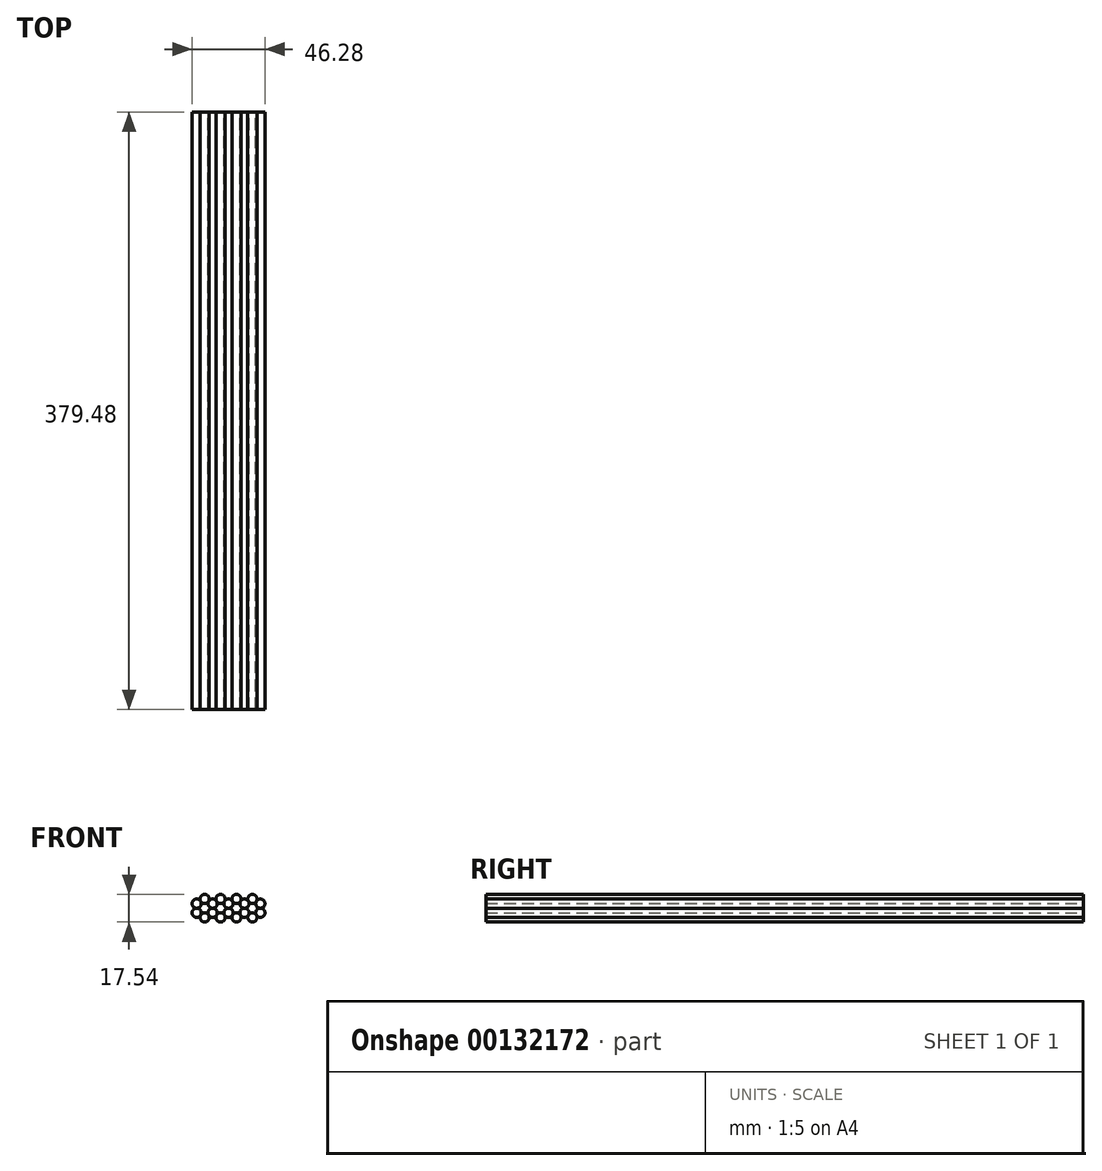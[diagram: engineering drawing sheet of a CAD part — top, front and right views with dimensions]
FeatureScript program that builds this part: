
annotation { "Feature Type Name" : "Feature", "Feature Type Description" : "" }
export const myFeature = defineFeature(function(context is Context, id is Id, definition is map)
    precondition{}
    {
        {
            var Q0;
            Q0=qCreatedBy(makeId("Front.planeOp"),FACE);
            var sketch = newSketch(context, id + "F0", { "sketchPlane" : qUnion([Q0])});
            skCircle(sketch, "E0", {"center": v(0, 0) * mm, "radius": 2.92 * mm});
            skCircle(sketch, "E1", {"center": v(5.05, 8.77) * mm, "radius": 2.92 * mm});
            skCircle(sketch, "E2", {"center": v(5.05, -2.93) * mm, "radius": 2.92 * mm});
            skCircle(sketch, "E3", {"center": v(10.1, 0) * mm, "radius": 2.92 * mm});
            skCircle(sketch, "E4", {"center": v(15.16, -2.93) * mm, "radius": 2.92 * mm});
            skCircle(sketch, "E5", {"center": v(10.1, 5.84) * mm, "radius": 2.92 * mm});
            skCircle(sketch, "E6", {"center": v(20.22, 0) * mm, "radius": 2.92 * mm});
            skCircle(sketch, "E7", {"center": v(20.22, 5.84) * mm, "radius": 2.92 * mm});
            skCircle(sketch, "E8", {"center": v(15.16, 8.77) * mm, "radius": 2.92 * mm});
            skCircle(sketch, "E9", {"center": v(-5.05, -2.93) * mm, "radius": 2.92 * mm});
            skCircle(sketch, "E10", {"center": v(0, 5.84) * mm, "radius": 2.92 * mm});
            skCircle(sketch, "E11", {"center": v(-5.05, 8.77) * mm, "radius": 2.92 * mm});
            skCircle(sketch, "E12", {"center": v(-10.1, 0) * mm, "radius": 2.92 * mm});
            skCircle(sketch, "E13", {"center": v(-15.16, 8.77) * mm, "radius": 2.92 * mm});
            skCircle(sketch, "E14", {"center": v(-10.1, 5.84) * mm, "radius": 2.92 * mm});
            skCircle(sketch, "E15", {"center": v(-20.22, 5.84) * mm, "radius": 2.92 * mm});
            skCircle(sketch, "E16", {"center": v(-20.22, 0) * mm, "radius": 2.92 * mm});
            skCircle(sketch, "E17", {"center": v(-15.16, -2.93) * mm, "radius": 2.92 * mm});
            skSolve(sketch);
        }
        {
            var Q0;
            {var subQ0=sQuery(id+"F0.wireOp",EDGE,"E6");var subQ1=makeQuery(id+"F0.imprint","INTERSECT",VERTEX,{"derivedFrom":[sQuery(id+"F0.wireOp",EDGE,"E4"),subQ0]});Q0=makeQuery(id+"F0.imprint","IMPRINT",FACE,{"disambiguationData":[TD([[makeQuery(id+"F0.imprint","IMPRINT",EDGE,{"disambiguationData":[TD([[subQ1,1.0]])],"derivedFrom":subQ0}),1.0]])]});}
            var Q1;
            {var subQ0=sQuery(id+"F0.wireOp",EDGE,"E4");var subQ1=makeQuery(id+"F0.imprint","INTERSECT",VERTEX,{"derivedFrom":[sQuery(id+"F0.wireOp",EDGE,"E3"),subQ0]});Q1=makeQuery(id+"F0.imprint","IMPRINT",FACE,{"disambiguationData":[TD([[makeQuery(id+"F0.imprint","IMPRINT",EDGE,{"disambiguationData":[TD([[subQ1,1.0]])],"derivedFrom":subQ0}),1.0]])]});}
            var Q2;
            {var subQ0=sQuery(id+"F0.wireOp",EDGE,"E2");var subQ1=makeQuery(id+"F0.imprint","INTERSECT",VERTEX,{"derivedFrom":[sQuery(id+"F0.wireOp",EDGE,"E0"),subQ0]});Q2=makeQuery(id+"F0.imprint","IMPRINT",FACE,{"disambiguationData":[TD([[makeQuery(id+"F0.imprint","IMPRINT",EDGE,{"disambiguationData":[TD([[subQ1,1.0]])],"derivedFrom":subQ0}),1.0]])]});}
            var Q3;
            {var subQ0=sQuery(id+"F0.wireOp",EDGE,"E1");var subQ1=makeQuery(id+"F0.imprint","INTERSECT",VERTEX,{"derivedFrom":[subQ0,sQuery(id+"F0.wireOp",EDGE,"E5")]});Q3=makeQuery(id+"F0.imprint","IMPRINT",FACE,{"disambiguationData":[TD([[makeQuery(id+"F0.imprint","IMPRINT",EDGE,{"disambiguationData":[TD([[subQ1,1.0]])],"derivedFrom":subQ0}),1.0]])]});}
            var Q4;
            {var subQ0=sQuery(id+"F0.wireOp",EDGE,"E11");var subQ1=makeQuery(id+"F0.imprint","INTERSECT",VERTEX,{"derivedFrom":[sQuery(id+"F0.wireOp",EDGE,"E10"),subQ0]});Q4=makeQuery(id+"F0.imprint","IMPRINT",FACE,{"disambiguationData":[TD([[makeQuery(id+"F0.imprint","IMPRINT",EDGE,{"disambiguationData":[TD([[subQ1,1.0]])],"derivedFrom":subQ0}),1.0]])]});}
            var Q5;
            {var subQ0=sQuery(id+"F0.wireOp",EDGE,"E5");var subQ1=makeQuery(id+"F0.imprint","INTERSECT",VERTEX,{"derivedFrom":[sQuery(id+"F0.wireOp",EDGE,"E1"),subQ0]});Q5=makeQuery(id+"F0.imprint","IMPRINT",FACE,{"disambiguationData":[TD([[makeQuery(id+"F0.imprint","IMPRINT",EDGE,{"disambiguationData":[TD([[subQ1,1.0]])],"derivedFrom":subQ0}),1.0]])]});}
            var Q6;
            {var subQ0=sQuery(id+"F0.wireOp",EDGE,"E12");var subQ1=makeQuery(id+"F0.imprint","INTERSECT",VERTEX,{"derivedFrom":[subQ0,sQuery(id+"F0.wireOp",EDGE,"E17")]});Q6=makeQuery(id+"F0.imprint","IMPRINT",FACE,{"disambiguationData":[TD([[makeQuery(id+"F0.imprint","IMPRINT",EDGE,{"disambiguationData":[TD([[subQ1,1.0]])],"derivedFrom":subQ0}),1.0]])]});}
            var Q7;
            {var subQ0=sQuery(id+"F0.wireOp",EDGE,"E9");var subQ1=makeQuery(id+"F0.imprint","INTERSECT",VERTEX,{"derivedFrom":[sQuery(id+"F0.wireOp",EDGE,"E0"),subQ0]});Q7=makeQuery(id+"F0.imprint","IMPRINT",FACE,{"disambiguationData":[TD([[makeQuery(id+"F0.imprint","IMPRINT",EDGE,{"disambiguationData":[TD([[subQ1,-1.0]])],"derivedFrom":subQ0}),1.0]])]});}
            var Q8;
            {var subQ0=sQuery(id+"F0.wireOp",EDGE,"E3");var subQ1=makeQuery(id+"F0.imprint","INTERSECT",VERTEX,{"derivedFrom":[sQuery(id+"F0.wireOp",EDGE,"E2"),subQ0]});Q8=makeQuery(id+"F0.imprint","IMPRINT",FACE,{"disambiguationData":[TD([[makeQuery(id+"F0.imprint","IMPRINT",EDGE,{"disambiguationData":[TD([[subQ1,1.0]])],"derivedFrom":subQ0}),1.0]])]});}
            var Q9;
            {var subQ0=sQuery(id+"F0.wireOp",EDGE,"E10");var subQ1=makeQuery(id+"F0.imprint","INTERSECT",VERTEX,{"derivedFrom":[subQ0,sQuery(id+"F0.wireOp",EDGE,"E11")]});Q9=makeQuery(id+"F0.imprint","IMPRINT",FACE,{"disambiguationData":[TD([[makeQuery(id+"F0.imprint","IMPRINT",EDGE,{"disambiguationData":[TD([[subQ1,-1.0]])],"derivedFrom":subQ0}),1.0]])]});}
            var Q10;
            {var subQ0=sQuery(id+"F0.wireOp",EDGE,"E14");var subQ1=makeQuery(id+"F0.imprint","INTERSECT",VERTEX,{"derivedFrom":[sQuery(id+"F0.wireOp",EDGE,"E11"),subQ0]});Q10=makeQuery(id+"F0.imprint","IMPRINT",FACE,{"disambiguationData":[TD([[makeQuery(id+"F0.imprint","IMPRINT",EDGE,{"disambiguationData":[TD([[subQ1,-1.0]])],"derivedFrom":subQ0}),1.0]])]});}
            var Q11;
            {var subQ0=sQuery(id+"F0.wireOp",EDGE,"E8");var subQ1=makeQuery(id+"F0.imprint","INTERSECT",VERTEX,{"derivedFrom":[sQuery(id+"F0.wireOp",EDGE,"E5"),subQ0]});Q11=makeQuery(id+"F0.imprint","IMPRINT",FACE,{"disambiguationData":[TD([[makeQuery(id+"F0.imprint","IMPRINT",EDGE,{"disambiguationData":[TD([[subQ1,-1.0]])],"derivedFrom":subQ0}),1.0]])]});}
            var Q12;
            {var subQ0=sQuery(id+"F0.wireOp",EDGE,"E17");var subQ1=makeQuery(id+"F0.imprint","INTERSECT",VERTEX,{"derivedFrom":[sQuery(id+"F0.wireOp",EDGE,"E12"),subQ0]});Q12=makeQuery(id+"F0.imprint","IMPRINT",FACE,{"disambiguationData":[TD([[makeQuery(id+"F0.imprint","IMPRINT",EDGE,{"disambiguationData":[TD([[subQ1,-1.0]])],"derivedFrom":subQ0}),1.0]])]});}
            var Q13;
            {var subQ0=sQuery(id+"F0.wireOp",EDGE,"E7");var subQ1=makeQuery(id+"F0.imprint","INTERSECT",VERTEX,{"derivedFrom":[sQuery(id+"F0.wireOp",EDGE,"E6"),subQ0]});Q13=makeQuery(id+"F0.imprint","IMPRINT",FACE,{"disambiguationData":[TD([[makeQuery(id+"F0.imprint","IMPRINT",EDGE,{"disambiguationData":[TD([[subQ1,1.0]])],"derivedFrom":subQ0}),1.0]])]});}
            var Q14;
            {var subQ0=sQuery(id+"F0.wireOp",EDGE,"E13");var subQ1=makeQuery(id+"F0.imprint","INTERSECT",VERTEX,{"derivedFrom":[subQ0,sQuery(id+"F0.wireOp",EDGE,"E14")]});Q14=makeQuery(id+"F0.imprint","IMPRINT",FACE,{"disambiguationData":[TD([[makeQuery(id+"F0.imprint","IMPRINT",EDGE,{"disambiguationData":[TD([[subQ1,1.0]])],"derivedFrom":subQ0}),1.0]])]});}
            var Q15;
            {var subQ0=sQuery(id+"F0.wireOp",EDGE,"E15");var subQ1=makeQuery(id+"F0.imprint","INTERSECT",VERTEX,{"derivedFrom":[sQuery(id+"F0.wireOp",EDGE,"E13"),subQ0]});Q15=makeQuery(id+"F0.imprint","IMPRINT",FACE,{"disambiguationData":[TD([[makeQuery(id+"F0.imprint","IMPRINT",EDGE,{"disambiguationData":[TD([[subQ1,-1.0]])],"derivedFrom":subQ0}),1.0]])]});}
            var Q16;
            {var subQ0=sQuery(id+"F0.wireOp",EDGE,"E16");var subQ1=makeQuery(id+"F0.imprint","INTERSECT",VERTEX,{"derivedFrom":[sQuery(id+"F0.wireOp",EDGE,"E15"),subQ0]});Q16=makeQuery(id+"F0.imprint","IMPRINT",FACE,{"disambiguationData":[TD([[makeQuery(id+"F0.imprint","IMPRINT",EDGE,{"disambiguationData":[TD([[subQ1,-1.0]])],"derivedFrom":subQ0}),1.0]])]});}
            var Q17;
            {var subQ0=sQuery(id+"F0.wireOp",EDGE,"E0");var subQ1=makeQuery(id+"F0.imprint","INTERSECT",VERTEX,{"derivedFrom":[subQ0,sQuery(id+"F0.wireOp",EDGE,"E9")]});Q17=makeQuery(id+"F0.imprint","IMPRINT",FACE,{"disambiguationData":[TD([[makeQuery(id+"F0.imprint","IMPRINT",EDGE,{"disambiguationData":[TD([[subQ1,1.0]])],"derivedFrom":subQ0}),1.0]])]});}
            extrude(context, id + "F1", {"entities" : qUnion([Q0, Q1, Q2, Q3, Q4, Q5, Q6, Q7, Q8, Q9, Q10, Q11, Q12, Q13, Q14, Q15, Q16, Q17]), "depth" : 379.48 * mm});
        }
    });
